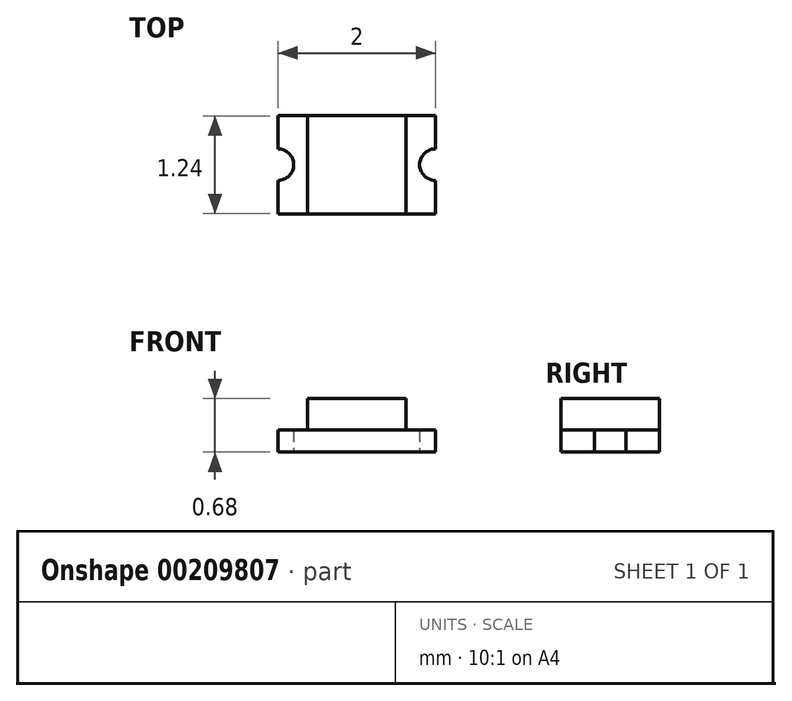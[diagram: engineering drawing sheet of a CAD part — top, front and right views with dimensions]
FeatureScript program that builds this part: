
annotation { "Feature Type Name" : "Feature", "Feature Type Description" : "" }
export const myFeature = defineFeature(function(context is Context, id is Id, definition is map)
    precondition{}
    {
        {
            var Q0;
            Q0=qCreatedBy(makeId("Top.planeOp"),FACE);
            var sketch = newSketch(context, id + "F0", { "sketchPlane" : qUnion([Q0]) });
            skLineSegment(sketch, "E0", {"start": v(0, 0.63) * mm, "end": v(-1, 0.62) * mm});
            skLineSegment(sketch, "E1", {"start": v(-1, 0.63) * mm, "end": v(-1, -0.63) * mm});
            skLineSegment(sketch, "E2", {"start": v(-1, -0.63) * mm, "end": v(0, -0.62) * mm});
            skCircle(sketch, "E3", {"center": v(-1, 0) * mm, "radius": 0.2 * mm});
            skLineSegment(sketch, "E4.MirrorCS", {"start": v(0, 0.62) * mm, "end": v(1, 0.63) * mm});
            skLineSegment(sketch, "E5.MirrorCS", {"start": v(1, 0.63) * mm, "end": v(1, -0.63) * mm});
            skCircle(sketch, "E6.MirrorC", {"center": v(1, 0) * mm, "radius": 0.2 * mm});
            skLineSegment(sketch, "E7.MirrorCS", {"start": v(1, -0.62) * mm, "end": v(0, -0.63) * mm});
            skSolve(sketch);
        }
        {
            var Q0;
            {var subQ8=sQuery(id+"F0.wireOp",EDGE,"E0");Q0=makeQuery(id+"F0.imprint","IMPRINT",FACE,{"disambiguationData":[TD([[makeQuery(id+"F0.imprint","IMPRINT",EDGE,{"derivedFrom":subQ8}),1.0]])]});}
            extrude(context, id + "F1", {"entities" : qUnion([Q0]), "depth" : 0.28 * mm});
        }
        {
            var Q0;
            Q0=makeQuery(id+"F1.opExtrude","CAP_FACE",FACE,{"disambiguationData":[OSD([sQuery(id+"F0.wireOp",EDGE,"E0"),sQuery(id+"F0.wireOp",EDGE,"E1"),sQuery(id+"F0.wireOp",EDGE,"E2"),sQuery(id+"F0.wireOp",EDGE,"E3"),sQuery(id+"F0.wireOp",EDGE,"E4.MirrorCS"),sQuery(id+"F0.wireOp",EDGE,"E5.MirrorCS"),sQuery(id+"F0.wireOp",EDGE,"E6.MirrorC"),sQuery(id+"F0.wireOp",EDGE,"E7.MirrorCS")])],"isStart":false});
            var sketch = newSketch(context, id + "F2", { "sketchPlane" : qUnion([Q0]) });
            skLineSegment(sketch, "E8.bottom", {"start": v(-0.62, 0.62) * mm, "end": v(0.62, 0.62) * mm});
            skLineSegment(sketch, "E8.top", {"start": v(-0.62, -0.62) * mm, "end": v(0.62, -0.62) * mm});
            skLineSegment(sketch, "E8.left", {"start": v(-0.62, 0.62) * mm, "end": v(-0.62, -0.62) * mm});
            skLineSegment(sketch, "E8.right", {"start": v(0.62, 0.62) * mm, "end": v(0.62, -0.62) * mm});
            skLineSegment(sketch, "E9", {"start": v(0, -0.62) * mm, "end": v(0, 0.62) * mm, "construction": true});
            skSolve(sketch);
        }
        {
            var Q0;
            Q0=makeQuery(id+"F2.imprint","IMPRINT",FACE,{"disambiguationData":[TD([[makeQuery(id+"F2.imprint","IMPRINT",EDGE,{"derivedFrom":sQuery(id+"F2.wireOp",EDGE,"E8.bottom")}),-1.0]])]});
            extrude(context, id + "F3", {"entities" : qUnion([Q0]), "depth" : 0.4 * mm});
        }
    });
